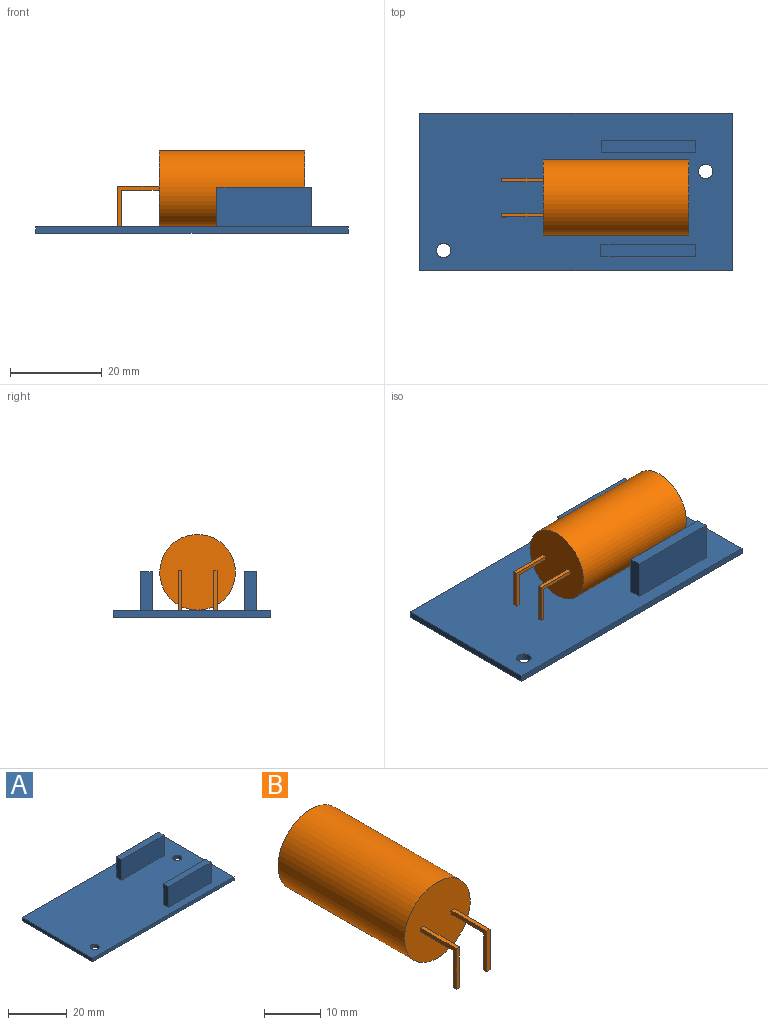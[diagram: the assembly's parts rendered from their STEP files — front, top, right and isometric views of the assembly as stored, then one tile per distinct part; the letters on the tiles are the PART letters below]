
ASSEMBLY  parts=2 mates=1
PART A: 18 faces, bbox 68x34.2x10 mm
  f0: plane 68x34.2mm, normal (0,0,1), area 2205.9mm2, adj f1,f2,f3,f4,f6,f7,f8,f9
  f1: plane 68x1.42mm, normal (0,-1,0), area 96.6mm2, adj f0,f2,f4,f5
  f2: plane 34.2x1.42mm, normal (1,0,0), area 48.6mm2, adj f0,f1,f3,f5
  f3: plane 68x1.42mm, normal (0,1,0), area 96.6mm2, adj f0,f2,f4,f5
  f4: plane 34.2x1.42mm, normal (-1,0,0), area 48.6mm2, adj f0,f1,f3,f5
  f5: plane 68x34.2mm, normal (0,0,-1), area 2310.1mm2, adj f1,f2,f3,f4,f16,f17
  f6: plane 20.55x8.52mm, normal (0,1,0), area 175.1mm2, adj f0,f7,f9,f10
  f7: plane 8.52x2.53mm, normal (-1,0,0), area 21.6mm2, adj f0,f6,f8,f10
  f8: plane 20.55x8.52mm, normal (0,-1,0), area 175.1mm2, adj f0,f7,f9,f10
  f9: plane 8.52x2.53mm, normal (1,0,0), area 21.6mm2, adj f0,f6,f8,f10
  f10: plane 20.55x2.53mm, normal (0,0,1), area 52mm2, adj f6,f7,f8,f9
  f11: plane 20.61x8.58mm, normal (0,1,0), area 176.8mm2, adj f0,f12,f14,f15
  f12: plane 8.58x2.53mm, normal (-1,0,0), area 21.7mm2, adj f0,f11,f13,f15
  f13: plane 20.61x8.58mm, normal (0,-1,0), area 176.8mm2, adj f0,f12,f14,f15
  f14: plane 8.58x2.53mm, normal (1,0,0), area 21.7mm2, adj f0,f11,f13,f15
  f15: plane 20.61x2.53mm, normal (0,0,1), area 52.1mm2, adj f11,f12,f13,f14
  f16: cylinder r=1.57mm len=3.15mm, axis (0,0,1), area 14.1mm2, adj f0,f5
  f17: cylinder r=1.57mm len=3.14mm, axis (0,0,1), area 14mm2, adj f0,f5
PART B: 17 faces, bbox 16.5x40.6x16.6 mm
  f0: plane 16.46x16.46mm, normal (0,-1,0), area 211.5mm2, adj f1,f3,f4,f5,f6,f8,f9,f10
  f1: cylinder r=8.23mm len=31.66mm, axis (0,1,0), area 1637.2mm2, adj f0,f2
  f2: plane 16.46x16.46mm, normal (0,1,0), area 212.8mm2, adj f1
  f3: plane 8.18x0.8mm, normal (0,0,-1), area 6.5mm2, adj f0,f4,f6,f13
  f4: plane 8.98x8.8mm, normal (1,0,0), area 13.6mm2, adj f0,f3,f5,f7,f13,f14
  f5: plane 8.98x0.8mm, normal (0,0,1), area 7.2mm2, adj f0,f4,f6,f7
  f6: plane 8.98x8.8mm, normal (-1,0,0), area 13.6mm2, adj f0,f3,f5,f7,f13,f14
  f7: plane 8.8x0.8mm, normal (0,-1,0), area 7mm2, adj f4,f5,f6,f14
  f8: plane 8.18x0.8mm, normal (0,0,-1), area 6.5mm2, adj f0,f9,f11,f15
  f9: plane 8.98x8.8mm, normal (1,0,0), area 13.6mm2, adj f0,f8,f10,f12,f15,f16
  f10: plane 8.98x0.8mm, normal (0,0,1), area 7.2mm2, adj f0,f9,f11,f12
  f11: plane 8.98x8.8mm, normal (-1,0,0), area 13.6mm2, adj f0,f8,f10,f12,f15,f16
  f12: plane 8.8x0.8mm, normal (0,-1,0), area 7mm2, adj f9,f10,f11,f16
  f13: plane 8x0.8mm, normal (0,1,0), area 6.4mm2, adj f3,f4,f6,f14
  f14: plane 0.8x0.8mm, normal (0,0,-1), area 0.6mm2, adj f4,f6,f7,f13
  f15: plane 8x0.8mm, normal (0,1,0), area 6.4mm2, adj f8,f9,f11,f16
  f16: plane 0.8x0.8mm, normal (0,0,-1), area 0.6mm2, adj f9,f11,f12,f15
PLACE A t=(-0.17,-0.09,-5.01)mm
PLACE B rot(axis=(0,0,-1),90deg) t=(24.33,-1.32,4.81)mm
MATE fastened B.f14 <-> A.f0  axis (0,0,-1) through (-15.91,2.5,-3.59)mm
